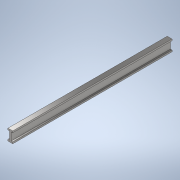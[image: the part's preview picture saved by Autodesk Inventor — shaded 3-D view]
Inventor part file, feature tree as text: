
AUTODESK INVENTOR PART (.ipt)
format: ipt  version: 2021 (Build 250183000, 183)  size: 138,240 bytes
history: native  units: in
note: dims shown in document units (in); Inventor stores cm internally (conversion verified against a paired STEP export)
features: extrude x1, sketch x1
ambient origin geometry x8: Origin, YZ Plane, XZ Plane, XY Plane, X Axis, Y Axis, Z Axis, Center Point
bodies: Solid1 (feature_tree)
feature tree (2):
  extrude  "Extrusion1"  Depth=0.7874in
  sketch  "Sketch1"  dims[d4=1.9685in d5=0.7874in d6=0.7874in d7=78.7402in d8=0.0in]
